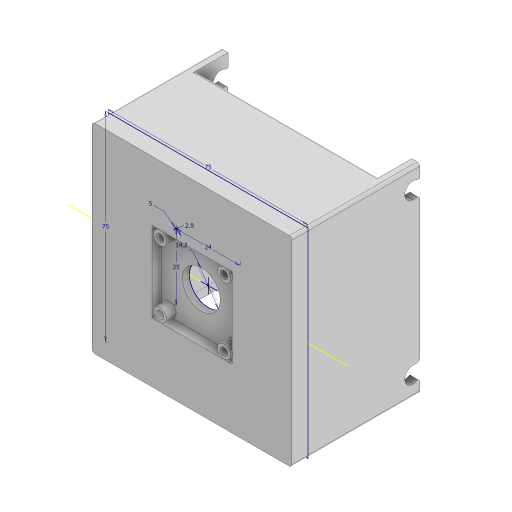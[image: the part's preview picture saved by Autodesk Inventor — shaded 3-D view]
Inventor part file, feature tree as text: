
AUTODESK INVENTOR PART (.ipt)
format: ipt  version: 2023 (Build 270158000, 158)  size: 229,376 bytes
history: native  units: mm
features: extrude x6, sketch x5, fillet x1, projected_geometry x1
ambient origin geometry x8: Origin, YZ Plane, XZ Plane, XY Plane, X Axis, Y Axis, Z Axis, Center Point
bodies: Solid1 (feature_tree)
feature tree (13):
  sketch  "Sketch1"  dims[d0=75.0mm d1=75.0mm]
  extrude  "Extrusion1"  Depth=75.0mm
  extrude  "Extrusion2"  Depth=5.0mm
  extrude  "Extrusion3"  Depth=20.0mm
  extrude  "Extrusion4"  Depth=6.0mm TaperAngle=0.0deg
  extrude  "Extrusion5"  Depth=1.0mm
  extrude  "Extrusion6"  Depth=1.0mm
  fillet  "Fillet2"  Radius=42.0mm
  sketch  "Sketch2"  dims[d2=14.2mm d3=5.0mm]
  sketch  "Sketch3"  dims[d4=2.9mm d5=20.0mm d7=24.0mm d8=20.0mm d10=25.0mm]
  projected_geometry  "Projected Loop1"
  sketch  "Sketch4"  dims[d13=2.5mm d14=0.0mm d15=6.0mm d16=0.0mm]
  sketch  "Sketch5"  dims[d18=6.1mm d19=6.1mm d20=60.0mm d21=42.0mm d22=1.0mm d23=3.0mm d24=0.0mm d25=3.0mm d26=0.0mm d27=30.0mm d28=30.0mm d29=3.0mm d30=0.0mm d31=1.0mm d32=2.5mm d33=30.0mm d34=0.0mm d36=1.0mm]
